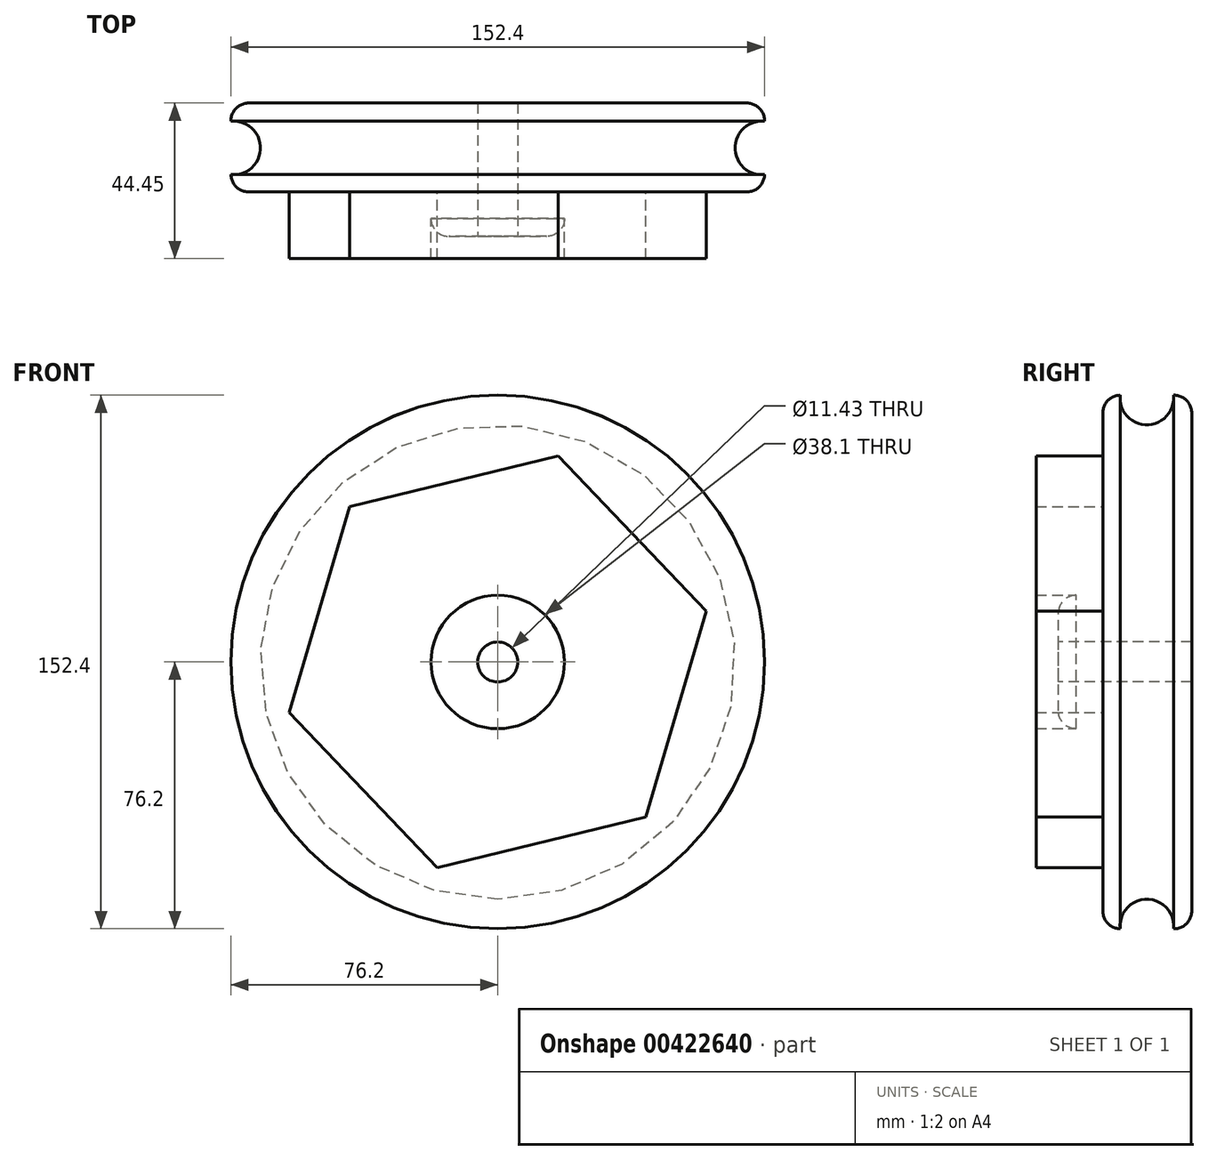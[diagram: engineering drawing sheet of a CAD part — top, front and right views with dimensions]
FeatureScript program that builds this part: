
annotation { "Feature Type Name" : "Feature", "Feature Type Description" : "" }
export const myFeature = defineFeature(function(context is Context, id is Id, definition is map)
    precondition{}
    {
        {
            var Q0;
            Q0=qCreatedBy(makeId("Front.planeOp"),FACE);
            var sketch = newSketch(context, id + "F0", { "sketchPlane" : qUnion([Q0])});
            skCircle(sketch, "E0", {"center": v(0, 0) * mm, "radius": 76.2 * mm});
            skSolve(sketch);
        }
        {
            var Q0;
            Q0=makeQuery(id+"F0.imprint","IMPRINT",FACE,{"disambiguationData":[TD([[makeQuery(id+"F0.imprint","IMPRINT",EDGE,{"derivedFrom":sQuery(id+"F0.wireOp",EDGE,"E0")}),1.0]])]});
            extrude(context, id + "F1", {"entities" : qUnion([Q0]), "depth" : 25.4 * mm});
        }
        {
            var Q0;
            Q0=makeQuery(id+"F1.opExtrude","CAP_FACE",FACE,{"disambiguationData":[OSD([sQuery(id+"F0.wireOp",EDGE,"E0")])],"isStart":false});
            var sketch = newSketch(context, id + "F2", { "sketchPlane" : qUnion([Q0])});
            skCircle(sketch, "E1", {"center": v(0, 0) * mm, "radius": 19.05 * mm});
            skSolve(sketch);
        }
        {
            var Q0;
            Q0=makeQuery(id+"F2.imprint","IMPRINT",FACE,{"disambiguationData":[TD([[makeQuery(id+"F2.imprint","IMPRINT",EDGE,{"derivedFrom":sQuery(id+"F2.wireOp",EDGE,"E1")}),1.0]])]});
            extrude(context, id + "F3", {"entities" : qUnion([Q0]), "operationType" : NewBodyOperationType.ADD, "depth" : 12.7 * mm});
        }
        {
            var Q0;
            Q0=makeQuery(id+"F3.opExtrude","CAP_FACE",FACE,{"disambiguationData":[OSD([sQuery(id+"F2.wireOp",EDGE,"E1")])],"isStart":false});
            fillet(context, id + "F4", {"entities" : qUnion([Q0]), "radius" : 5.08 * mm, "tangentPropagation" : true, "allowEdgeOverflow" : false});
        }
        {
            var Q0;
            Q0=makeQuery(id+"F1.opExtrude","SWEPT_FACE",FACE,{"disambiguationData":[OSD([sQuery(id+"F0.wireOp",EDGE,"E0")])]});
            fillet(context, id + "F5", {"entities" : qUnion([Q0]), "radius" : 5.08 * mm, "tangentPropagation" : true, "allowEdgeOverflow" : false});
        }
        {
            var Q0;
            Q0=makeQuery(id+"F3.opExtrude","CAP_FACE",FACE,{"disambiguationData":[OSD([sQuery(id+"F2.wireOp",EDGE,"E1")])],"isStart":false});
            var sketch = newSketch(context, id + "F6", { "sketchPlane" : qUnion([Q0])});
            skCircle(sketch, "E2", {"center": v(0, 0) * mm, "radius": 5.72 * mm});
            skSolve(sketch);
        }
        {
            var Q0;
            Q0=makeQuery(id+"F6.imprint","IMPRINT",FACE,{"disambiguationData":[TD([[makeQuery(id+"F6.imprint","IMPRINT",EDGE,{"derivedFrom":sQuery(id+"F6.wireOp",EDGE,"E2")}),1.0]])]});
            var Q1;
            Q1=sQuery(id+"F6.wireOp",EDGE,"E2");
            extrude(context, id + "F7", {"entities" : qUnion([Q0]), "operationType" : NewBodyOperationType.REMOVE, "surfaceEntities" : qUnion([Q1]), "oppositeDirection" : true, "depth" : 129.03 * mm});
        }
        {
            var Q0;
            Q0=qCreatedBy(makeId("Right.planeOp"),FACE);
            var sketch = newSketch(context, id + "F8", { "sketchPlane" : qUnion([Q0])});
            skCircle(sketch, "E3", {"center": v(-12.82, 75.42) * mm, "radius": 7.66 * mm});
            skPoint(sketch, "E3.first.point", {"position": v(-20.4, 76.51) * mm});
            skPoint(sketch, "E3.second.point", {"position": v(-5.25, 76.51) * mm});
            skPoint(sketch, "E3.third.point", {"position": v(-12.53, 67.77) * mm});
            skSolve(sketch);
        }
        {
            var Q0;
            Q0 = qSketchRegion(id + "F8", true);
            var Q1;
            {var subQ0=sQuery(id+"F0.wireOp",EDGE,"E0");Q1=makeQuery(id+"F5.opFillet","BLEND_EDGE",EDGE,{"blendedFrom":[makeQuery(id+"F1.opExtrude","CAP_EDGE",EDGE,{"disambiguationData":[OSD([subQ0])],"isStart":false}),makeQuery(id+"F1.opExtrude","CAP_FACE",FACE,{"disambiguationData":[OSD([subQ0])],"isStart":false})],"blendedInto":[makeQuery(id+"F1.opExtrude","CAP_FACE",FACE,{"disambiguationData":[OSD([subQ0])],"isStart":false})]});}
            revolve(context, id + "F9", {"operationType" : NewBodyOperationType.REMOVE, "entities" : qUnion([Q0]), "axis" : qUnion([Q1]), "revolveType" : RevolveType.FULL, "oppositeDirection" : true});
        }
        {
            var Q0;
            Q0=makeQuery(id+"F1.opExtrude","CAP_FACE",FACE,{"disambiguationData":[OSD([sQuery(id+"F0.wireOp",EDGE,"E0")])],"isStart":false});
            var sketch = newSketch(context, id + "F10", { "sketchPlane" : qUnion([Q0])});
            skCircle(sketch, "E4.cCircle", {"center": v(0, 0) * mm, "radius": 53.07 * mm, "construction": true});
            skLineSegment(sketch, "E4.0", {"start": v(59.55, 14.47) * mm, "end": v(42.3, -44.34) * mm});
            skLineSegment(sketch, "E4.1", {"start": v(42.3, -44.34) * mm, "end": v(-17.24, -58.8) * mm});
            skLineSegment(sketch, "E4.2", {"start": v(-17.24, -58.8) * mm, "end": v(-59.55, -14.47) * mm});
            skLineSegment(sketch, "E4.3", {"start": v(-59.55, -14.47) * mm, "end": v(-42.3, 44.34) * mm});
            skLineSegment(sketch, "E4.4", {"start": v(-42.3, 44.34) * mm, "end": v(17.24, 58.8) * mm});
            skLineSegment(sketch, "E4.5", {"start": v(17.24, 58.8) * mm, "end": v(59.55, 14.47) * mm});
            skPoint(sketch, "E4.0.midPoint", {"position": v(50.93, -14.93) * mm});
            skSolve(sketch);
        }
        {
            var Q0;
            Q0=makeQuery(id+"F10.imprint","IMPRINT",FACE,{"disambiguationData":[TD([[makeQuery(id+"F10.imprint","IMPRINT",EDGE,{"derivedFrom":sQuery(id+"F10.wireOp",EDGE,"E4.0")}),-1.0]])]});
            extrude(context, id + "F11", {"entities" : qUnion([Q0]), "operationType" : NewBodyOperationType.ADD, "depth" : 19.05 * mm, "offsetDistance" : 25.4 * mm});
        }
    });
